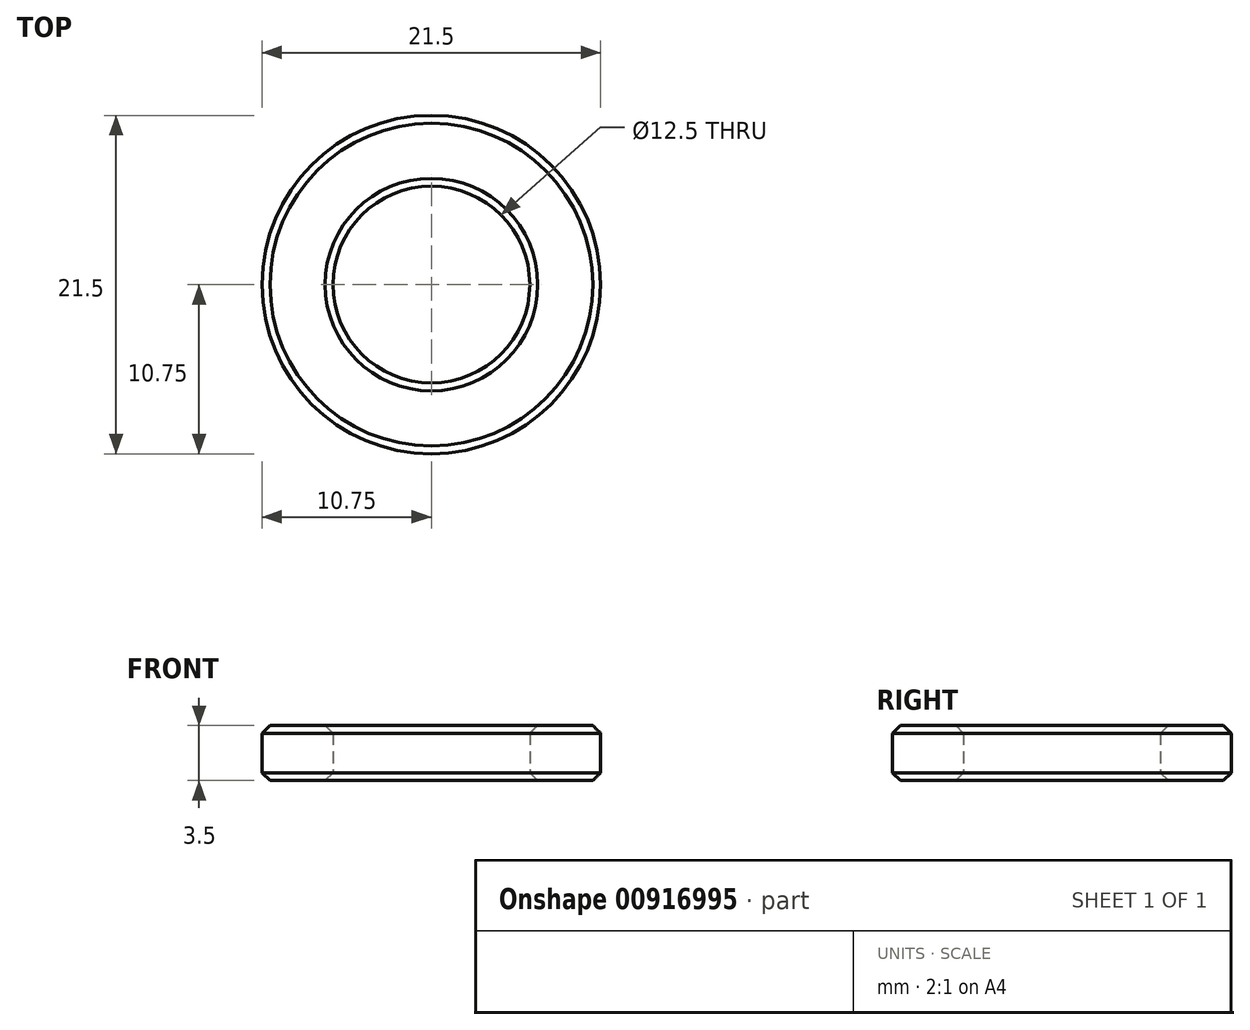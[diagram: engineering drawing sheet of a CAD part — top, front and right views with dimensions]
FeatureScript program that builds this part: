
annotation { "Feature Type Name" : "Feature", "Feature Type Description" : "" }
export const myFeature = defineFeature(function(context is Context, id is Id, definition is map)
    precondition{}
    {
        {
            var Q0;
            Q0=qCreatedBy(makeId("Top.planeOp"),FACE);
            var sketch = newSketch(context, id + "F0", { "sketchPlane" : qUnion([Q0])});
            skCircle(sketch, "E0", {"center": v(0, 0) * mm, "radius": 10.75 * mm});
            skCircle(sketch, "E1", {"center": v(0, 0) * mm, "radius": 6.25 * mm});
            skSolve(sketch);
        }
        {
            var Q0;
            Q0=makeQuery(id+"F0.imprint","IMPRINT",FACE,{"disambiguationData":[TD([[makeQuery(id+"F0.imprint","IMPRINT",EDGE,{"derivedFrom":sQuery(id+"F0.wireOp",EDGE,"E0")}),1.0]])]});
            extrude(context, id + "F1", {"entities" : qUnion([Q0]), "depth" : 3.5 * mm, "offsetDistance" : 25 * mm});
        }
        {
            var Q0;
            Q0=makeQuery(id+"F1.opExtrude","CAP_EDGE",EDGE,{"disambiguationData":[OSD([sQuery(id+"F0.wireOp",EDGE,"E1")])],"isStart":false});
            var Q1;
            Q1=makeQuery(id+"F1.opExtrude","CAP_EDGE",EDGE,{"disambiguationData":[OSD([sQuery(id+"F0.wireOp",EDGE,"E1")])],"isStart":true});
            var Q2;
            Q2=makeQuery(id+"F1.opExtrude","CAP_EDGE",EDGE,{"disambiguationData":[OSD([sQuery(id+"F0.wireOp",EDGE,"E0")])],"isStart":false});
            var Q3;
            Q3=makeQuery(id+"F1.opExtrude","CAP_EDGE",EDGE,{"disambiguationData":[OSD([sQuery(id+"F0.wireOp",EDGE,"E0")])],"isStart":true});
            chamfer(context, id + "F2", {"entities" : qUnion([Q0, Q1, Q2, Q3]), "width" : .5 * mm, "tangentPropagation" : true});
        }
    });
